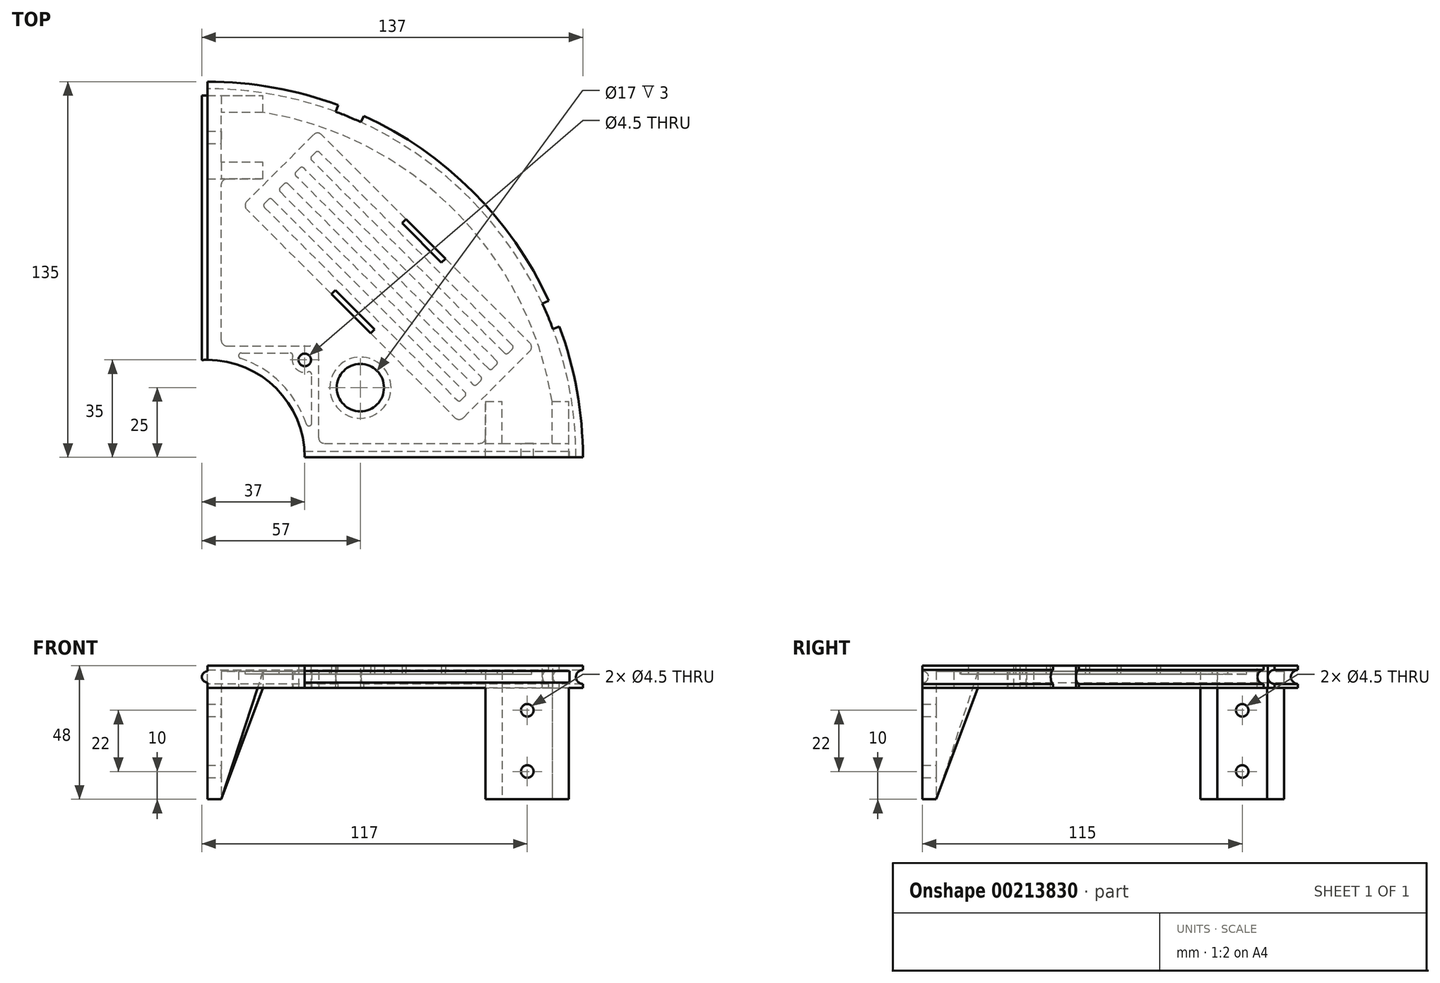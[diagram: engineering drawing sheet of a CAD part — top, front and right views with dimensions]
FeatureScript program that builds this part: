
annotation { "Feature Type Name" : "Feature", "Feature Type Description" : "" }
export const myFeature = defineFeature(function(context is Context, id is Id, definition is map)
    precondition{}
    {
        {
            var Q0;
            Q0=qCreatedBy(makeId("Top.planeOp"),FACE);
            var sketch = newSketch(context, id + "F0", { "sketchPlane" : qUnion([Q0])});
            skArc(sketch, "E0", {"start": v(135, 0) * mm, "mid": v(95.46, 95.46) * mm, "end": v(0, 135) * mm});
            skArc(sketch, "E1", {"start": v(35, 0) * mm, "mid": v(24.75, 24.75) * mm, "end": v(0, 35) * mm});
            skLineSegment(sketch, "E2.trimOffspring", {"start": v(35, 0) * mm, "end": v(135, 0) * mm});
            skLineSegment(sketch, "E3.1.5", {"start": v(0, 35) * mm, "end": v(0, 135) * mm});
            skCircle(sketch, "E4", {"center": v(35, 35) * mm, "radius": 2.25 * mm});
            skSolve(sketch);
        }
        {
            var Q0;
            Q0=qSketchRegion(id+"F0",true);
            extrude(context, id + "F1", {"entities" : qUnion([Q0]), "depth" : 8 * mm});
        }
        {
            var Q0;
            Q0=qCreatedBy(makeId("Top.planeOp"),FACE);
            cPlane(context, id + "F2", {"entities" : qUnion([Q0]), "cplaneType" : CPlaneType.OFFSET, "offset" : 4 * mm, "width" : 150 * mm, "height" : 150 * mm});
        }
        {
            var Q0;
            Q0=qCreatedBy(id+"F2.planeOp",FACE);
            var sketch = newSketch(context, id + "F3", { "sketchPlane" : qUnion([Q0])});
            skCircle(sketch, "E5", {"center": v(0, 0) * mm, "radius": 135 * mm});
            skSolve(sketch);
        }
        {
            var Q0;
            Q0=makeQuery(id+"F1.opExtrude","SWEPT_FACE",FACE,{"disambiguationData":[OSD([sQuery(id+"F0.wireOp",EDGE,"E2.trimOffspring")])]});
            var sketch = newSketch(context, id + "F4", { "sketchPlane" : qUnion([Q0])});
            skCircle(sketch, "E6", {"center": v(135, 4) * mm, "radius": 2.5 * mm});
            skSolve(sketch);
        }
        {
            var Q0;
            Q0=qSketchRegion(id+"F4",true);
            var Q1;
            Q1=qConstructionFilter(qBodyType(qCreatedBy(id+"F3",EDGE),BodyType.WIRE),ConstructionObject.NO);
            sweep(context, id + "F5", {"operationType" : NewBodyOperationType.REMOVE, "profiles" : qUnion([Q0]), "path" : qUnion([Q1])});
        }
        {
            var Q0;
            Q0=makeQuery(id+"F1.opExtrude","CAP_FACE",FACE,{"disambiguationData":[OSD([sQuery(id+"F0.wireOp",EDGE,"E0"),sQuery(id+"F0.wireOp",EDGE,"E1"),sQuery(id+"F0.wireOp",EDGE,"E2.trimOffspring"),sQuery(id+"F0.wireOp",EDGE,"E3.1.5"),sQuery(id+"F0.wireOp",EDGE,"E4")])],"isStart":true});
            var sketch = newSketch(context, id + "F6", { "sketchPlane" : qUnion([Q0])});
            skLineSegment(sketch, "E7.bottom", {"start": v(100, 0) * mm, "end": v(130, 0) * mm});
            skLineSegment(sketch, "E7.top", {"start": v(100, -20) * mm, "end": v(130, -20) * mm});
            skLineSegment(sketch, "E7.left", {"start": v(100, 0) * mm, "end": v(100, -20) * mm});
            skLineSegment(sketch, "E7.right", {"start": v(130, 0) * mm, "end": v(130, -20) * mm});
            skLineSegment(sketch, "E8.bottom", {"start": v(0, -100) * mm, "end": v(20, -100) * mm});
            skLineSegment(sketch, "E8.top", {"start": v(0, -130) * mm, "end": v(20, -130) * mm});
            skLineSegment(sketch, "E8.left", {"start": v(0, -100) * mm, "end": v(0, -130) * mm});
            skLineSegment(sketch, "E8.right", {"start": v(20, -100) * mm, "end": v(20, -130) * mm});
            skSolve(sketch);
        }
        {
            var Q0;
            Q0=qSketchRegion(id+"F6",true);
            extrude(context, id + "F7", {"entities" : qUnion([Q0]), "operationType" : NewBodyOperationType.ADD, "depth" : 40 * mm});
        }
        {
            var Q0;
            Q0=makeQuery(id+"F7.opExtrude","CAP_FACE",FACE,{"disambiguationData":[OSD([sQuery(id+"F6.wireOp",EDGE,"E7.bottom"),sQuery(id+"F6.wireOp",EDGE,"E7.top"),sQuery(id+"F6.wireOp",EDGE,"E7.left"),sQuery(id+"F6.wireOp",EDGE,"E7.right")])],"isStart":false});
            var sketch = newSketch(context, id + "F8", { "sketchPlane" : qUnion([Q0])});
            skLineSegment(sketch, "E9.bottom", {"start": v(106, -5) * mm, "end": v(124, -5) * mm});
            skLineSegment(sketch, "E9.top", {"start": v(106, -20) * mm, "end": v(124, -20) * mm});
            skLineSegment(sketch, "E9.left", {"start": v(106, -5) * mm, "end": v(106, -20) * mm});
            skLineSegment(sketch, "E9.right", {"start": v(124, -5) * mm, "end": v(124, -20) * mm});
            skLineSegment(sketch, "E10.bottom", {"start": v(20, -106) * mm, "end": v(5, -106) * mm});
            skLineSegment(sketch, "E10.top", {"start": v(20, -124) * mm, "end": v(5, -124) * mm});
            skLineSegment(sketch, "E10.left", {"start": v(20, -106) * mm, "end": v(20, -124) * mm});
            skLineSegment(sketch, "E10.right", {"start": v(5, -106) * mm, "end": v(5, -124) * mm});
            skSolve(sketch);
        }
        {
            var Q0;
            Q0=qSketchRegion(id+"F8",true);
            extrude(context, id + "F9", {"entities" : qUnion([Q0]), "operationType" : NewBodyOperationType.REMOVE, "oppositeDirection" : true, "depth" : 40 * mm});
        }
        {
            var Q0;
            {var subQ0=sQuery(id+"F6.wireOp",EDGE,"E7.right");var subQ1=sQuery(id+"F6.wireOp",EDGE,"E7.top");Q0=makeQuery(id+"F9.boolean.opBoolean","SPLIT",EDGE,{"disambiguationData":[TD([makeQuery(id+"F7.opExtrude","SWEPT_FACE",FACE,{"disambiguationData":[OSD([subQ0])]})])],"derivedFrom":makeQuery(id+"F7.opExtrude","CAP_EDGE",EDGE,{"disambiguationData":[OSD([subQ1])],"isStart":false})});}
            chamfer(context, id + "F10", {"entities" : qUnion([Q0]), "chamferType" : ChamferType.TWO_OFFSETS, "width1" : 15 * mm, "oppositeDirection" : false, "width2" : 40 * mm, "tangentPropagation" : true});
        }
        {
            var Q0;
            Q0=makeQuery(id+"F9.boolean.opBoolean","COPY",FACE,{"derivedFrom":makeQuery(id+"F9.opExtrude","SWEPT_FACE",FACE,{"disambiguationData":[OSD([sQuery(id+"F8.wireOp",EDGE,"E9.bottom")])]})});
            var sketch = newSketch(context, id + "F11", { "sketchPlane" : qUnion([Q0])});
            skCircle(sketch, "E11", {"center": v(-115, -8) * mm, "radius": 2.25 * mm});
            skCircle(sketch, "E12", {"center": v(-115, -30) * mm, "radius": 2.25 * mm});
            skSolve(sketch);
        }
        {
            var Q0;
            Q0=qSketchRegion(id+"F11",true);
            extrude(context, id + "F12", {"entities" : qUnion([Q0]), "operationType" : NewBodyOperationType.REMOVE, "oppositeDirection" : true, "depth" : 25 * mm});
        }
        {
            var Q0;
            {var subQ0=sQuery(id+"F6.wireOp",EDGE,"E8.right");var subQ1=sQuery(id+"F6.wireOp",EDGE,"E8.top");Q0=makeQuery(id+"F9.boolean.opBoolean","SPLIT",EDGE,{"disambiguationData":[TD([makeQuery(id+"F7.opExtrude","SWEPT_FACE",FACE,{"disambiguationData":[OSD([subQ1])]})])],"derivedFrom":makeQuery(id+"F7.opExtrude","CAP_EDGE",EDGE,{"disambiguationData":[OSD([subQ0])],"isStart":false})});}
            chamfer(context, id + "F13", {"entities" : qUnion([Q0]), "chamferType" : ChamferType.TWO_OFFSETS, "width1" : 40 * mm, "oppositeDirection" : false, "width2" : 15 * mm, "tangentPropagation" : true});
        }
        {
            var Q0;
            Q0=makeQuery(id+"F9.boolean.opBoolean","COPY",FACE,{"derivedFrom":makeQuery(id+"F9.opExtrude","SWEPT_FACE",FACE,{"disambiguationData":[OSD([sQuery(id+"F8.wireOp",EDGE,"E10.right")])]})});
            var sketch = newSketch(context, id + "F14", { "sketchPlane" : qUnion([Q0])});
            skCircle(sketch, "E13", {"center": v(115, -30) * mm, "radius": 2.25 * mm});
            skCircle(sketch, "E14", {"center": v(115, -8) * mm, "radius": 2.25 * mm});
            skSolve(sketch);
        }
        {
            var Q0;
            Q0=qSketchRegion(id+"F14",true);
            extrude(context, id + "F15", {"entities" : qUnion([Q0]), "operationType" : NewBodyOperationType.REMOVE, "oppositeDirection" : true, "depth" : 25 * mm});
        }
        {
            var Q0;
            Q0=makeQuery(id+"F1.opExtrude","CAP_FACE",FACE,{"disambiguationData":[OSD([sQuery(id+"F0.wireOp",EDGE,"E0"),sQuery(id+"F0.wireOp",EDGE,"E1"),sQuery(id+"F0.wireOp",EDGE,"E2.trimOffspring"),sQuery(id+"F0.wireOp",EDGE,"E3.1.5"),sQuery(id+"F0.wireOp",EDGE,"E4")])],"isStart":false});
            var sketch = newSketch(context, id + "F16", { "sketchPlane" : qUnion([Q0])});
            skArc(sketch, "E15", {"start": v(124.2, 46.14) * mm, "mid": v(122.41, 50.71) * mm, "end": v(120.45, 55.2) * mm});
            skArc(sketch, "E16", {"start": v(126.55, 47.01) * mm, "mid": v(124.72, 51.67) * mm, "end": v(122.72, 56.25) * mm});
            skLineSegment(sketch, "E17", {"start": v(0, 0) * mm, "end": v(124.72, 51.66) * mm, "construction": true});
            skLineSegment(sketch, "E18", {"start": v(0, 0) * mm, "end": v(51.66, 124.72) * mm, "construction": true});
            skLineSegment(sketch, "E19", {"start": v(46.13, 124.21) * mm, "end": v(47, 126.55) * mm});
            skLineSegment(sketch, "E20", {"start": v(124.2, 46.14) * mm, "end": v(126.55, 47.01) * mm});
            skLineSegment(sketch, "E21", {"start": v(55.2, 120.45) * mm, "end": v(56.24, 122.73) * mm});
            skLineSegment(sketch, "E22", {"start": v(120.45, 55.2) * mm, "end": v(122.72, 56.25) * mm});
            skArc(sketch, "E23.trimOffspring", {"start": v(56.24, 122.73) * mm, "mid": v(51.66, 124.73) * mm, "end": v(47, 126.55) * mm});
            skArc(sketch, "E24.trimOffspring", {"start": v(55.2, 120.45) * mm, "mid": v(50.7, 122.42) * mm, "end": v(46.13, 124.21) * mm});
            skSolve(sketch);
        }
        {
            var Q0;
            Q0=qSketchRegion(id+"F16",true);
            extrude(context, id + "F17", {"entities" : qUnion([Q0]), "operationType" : NewBodyOperationType.REMOVE, "oppositeDirection" : true, "depth" : 25 * mm});
        }
        {
            var Q0;
            Q0=makeQuery(id+"F9.boolean.opBoolean","MERGE",FACE,{"derivedFrom":[makeQuery(id+"F1.opExtrude","CAP_FACE",FACE,{"disambiguationData":[OSD([sQuery(id+"F0.wireOp",EDGE,"E0"),sQuery(id+"F0.wireOp",EDGE,"E1"),sQuery(id+"F0.wireOp",EDGE,"E2.trimOffspring"),sQuery(id+"F0.wireOp",EDGE,"E3.1.5"),sQuery(id+"F0.wireOp",EDGE,"E4")])],"isStart":true}),makeQuery(id+"F9.opExtrude","CAP_FACE",FACE,{"disambiguationData":[OSD([sQuery(id+"F8.wireOp",EDGE,"E9.bottom"),sQuery(id+"F8.wireOp",EDGE,"E9.top"),sQuery(id+"F8.wireOp",EDGE,"E9.left"),sQuery(id+"F8.wireOp",EDGE,"E9.right")])],"isStart":false}),makeQuery(id+"F9.opExtrude","CAP_FACE",FACE,{"disambiguationData":[OSD([sQuery(id+"F8.wireOp",EDGE,"E10.bottom"),sQuery(id+"F8.wireOp",EDGE,"E10.top"),sQuery(id+"F8.wireOp",EDGE,"E10.left"),sQuery(id+"F8.wireOp",EDGE,"E10.right")])],"isStart":false})]});
            var sketch = newSketch(context, id + "F18", { "sketchPlane" : qUnion([Q0])});
            skLineSegment(sketch, "E25", {"start": v(0, 0) * mm, "end": v(106.07, -106.07) * mm, "construction": true});
            skLineSegment(sketch, "E26", {"start": v(45.96, -60.1) * mm, "end": v(60.1, -45.96) * mm});
            skLineSegment(sketch, "E27", {"start": v(70, -84.15) * mm, "end": v(84.15, -70) * mm});
            skLineSegment(sketch, "E28", {"start": v(44.55, -58.69) * mm, "end": v(58.69, -44.55) * mm});
            skLineSegment(sketch, "E29", {"start": v(71.42, -85.56) * mm, "end": v(85.56, -71.42) * mm});
            skLineSegment(sketch, "E30", {"start": v(44.55, -58.69) * mm, "end": v(45.96, -60.1) * mm});
            skLineSegment(sketch, "E31", {"start": v(58.69, -44.55) * mm, "end": v(60.1, -45.96) * mm});
            skLineSegment(sketch, "E32", {"start": v(84.15, -70) * mm, "end": v(85.56, -71.42) * mm});
            skLineSegment(sketch, "E33", {"start": v(70, -84.15) * mm, "end": v(71.42, -85.56) * mm});
            skSolve(sketch);
        }
        {
            var Q0;
            Q0=qSketchRegion(id+"F18",true);
            extrude(context, id + "F19", {"entities" : qUnion([Q0]), "operationType" : NewBodyOperationType.REMOVE, "endBound" : BoundingType.THROUGH_ALL, "oppositeDirection" : true, "depth" : 7.8 * mm});
        }
        {
            var Q0;
            Q0=makeQuery(id+"F7.boolean.opBoolean","MERGE",FACE,{"derivedFrom":[makeQuery(id+"F1.opExtrude","SWEPT_FACE",FACE,{"disambiguationData":[OSD([sQuery(id+"F0.wireOp",EDGE,"E2.trimOffspring")])]}),makeQuery(id+"F7.opExtrude","SWEPT_FACE",FACE,{"disambiguationData":[OSD([sQuery(id+"F6.wireOp",EDGE,"E7.bottom")])]})]});
            var sketch = newSketch(context, id + "F20", { "sketchPlane" : qUnion([Q0])});
            skLineSegment(sketch, "E34", {"start": v(0, 4) * mm, "end": v(130.2, 4) * mm});
            skSolve(sketch);
        }
        {
            var Q0;
            Q0=makeQuery(id+"F7.boolean.opBoolean","MERGE",FACE,{"derivedFrom":[makeQuery(id+"F1.opExtrude","SWEPT_FACE",FACE,{"disambiguationData":[OSD([sQuery(id+"F0.wireOp",EDGE,"E3.1.5")])]}),makeQuery(id+"F7.opExtrude","SWEPT_FACE",FACE,{"disambiguationData":[OSD([sQuery(id+"F6.wireOp",EDGE,"E8.left")])]})]});
            var sketch = newSketch(context, id + "F21", { "sketchPlane" : qUnion([Q0])});
            skLineSegment(sketch, "E35", {"start": v(-130, 4) * mm, "end": v(0, 4) * mm});
            skSolve(sketch);
        }
        {
            var Q0;
            Q0=qCreatedBy(makeId("Front.planeOp"),FACE);
            var sketch = newSketch(context, id + "F22", { "sketchPlane" : qUnion([Q0])});
            skCircle(sketch, "E36", {"center": v(0, 4) * mm, "radius": 2 * mm});
            skSolve(sketch);
        }
        {
            var Q0;
            Q0=makeQuery(id+"F22.imprint","IMPRINT",FACE,{"disambiguationData":[TD([[makeQuery(id+"F22.imprint","IMPRINT",EDGE,{"derivedFrom":sQuery(id+"F22.wireOp",EDGE,"E36")}),1.0]])]});
            var Q1;
            Q1=sQuery(id+"F21.wireOp",EDGE,"E35");
            sweep(context, id + "F23", {"operationType" : NewBodyOperationType.ADD, "profiles" : qUnion([Q0]), "path" : qUnion([Q1])});
        }
        {
            var Q0;
            Q0=makeQuery(id+"F1.opExtrude","CAP_FACE",FACE,{"disambiguationData":[OSD([sQuery(id+"F0.wireOp",EDGE,"E0"),sQuery(id+"F0.wireOp",EDGE,"E1"),sQuery(id+"F0.wireOp",EDGE,"E2.trimOffspring"),sQuery(id+"F0.wireOp",EDGE,"E3.1.5"),sQuery(id+"F0.wireOp",EDGE,"E4")])],"isStart":false});
            var sketch = newSketch(context, id + "F24", { "sketchPlane" : qUnion([Q0])});
            skCircle(sketch, "E37", {"center": v(0, 0) * mm, "radius": 35 * mm});
            skSolve(sketch);
        }
        {
            var Q0;
            {var subQ0=sQuery(id+"F24.wireOp",EDGE,"E37");var subQ1=makeQuery(id+"F24.imprint","INTERSECT",VERTEX,{"derivedFrom":[makeQuery(id+"F1.opExtrude","CAP_EDGE",EDGE,{"disambiguationData":[OSD([sQuery(id+"F0.wireOp",EDGE,"E2.trimOffspring")])],"isStart":false}),subQ0]});Q0=makeQuery(id+"F24.imprint","IMPRINT",FACE,{"disambiguationData":[TD([[makeQuery(id+"F24.imprint","IMPRINT",EDGE,{"disambiguationData":[TD([[subQ1,-1.0]])],"derivedFrom":subQ0}),1.0]])]});}
            extrude(context, id + "F25", {"entities" : qUnion([Q0]), "operationType" : NewBodyOperationType.REMOVE, "endBound" : BoundingType.THROUGH_ALL, "oppositeDirection" : true, "depth" : 25 * mm});
        }
        {
            var Q0;
            Q0=qCreatedBy(makeId("Right.planeOp"),FACE);
            var sketch = newSketch(context, id + "F26", { "sketchPlane" : qUnion([Q0])});
            skCircle(sketch, "E38", {"center": v(0, 4) * mm, "radius": 2.1 * mm});
            skSolve(sketch);
        }
        {
            var Q0;
            Q0=makeQuery(id+"F26.imprint","IMPRINT",FACE,{"disambiguationData":[TD([[makeQuery(id+"F26.imprint","IMPRINT",EDGE,{"derivedFrom":sQuery(id+"F26.wireOp",EDGE,"E38")}),1.0]])]});
            var Q1;
            Q1=sQuery(id+"F20.wireOp",EDGE,"E34");
            sweep(context, id + "F27", {"operationType" : NewBodyOperationType.REMOVE, "profiles" : qUnion([Q0]), "path" : qUnion([Q1])});
        }
        {
            var Q0;
            Q0=makeQuery(id+"F9.boolean.opBoolean","MERGE",FACE,{"derivedFrom":[makeQuery(id+"F1.opExtrude","CAP_FACE",FACE,{"disambiguationData":[OSD([sQuery(id+"F0.wireOp",EDGE,"E0"),sQuery(id+"F0.wireOp",EDGE,"E1"),sQuery(id+"F0.wireOp",EDGE,"E2.trimOffspring"),sQuery(id+"F0.wireOp",EDGE,"E3.1.5"),sQuery(id+"F0.wireOp",EDGE,"E4")])],"isStart":true}),makeQuery(id+"F9.opExtrude","CAP_FACE",FACE,{"disambiguationData":[OSD([sQuery(id+"F8.wireOp",EDGE,"E9.bottom"),sQuery(id+"F8.wireOp",EDGE,"E9.top"),sQuery(id+"F8.wireOp",EDGE,"E9.left"),sQuery(id+"F8.wireOp",EDGE,"E9.right")])],"isStart":false}),makeQuery(id+"F9.opExtrude","CAP_FACE",FACE,{"disambiguationData":[OSD([sQuery(id+"F8.wireOp",EDGE,"E10.bottom"),sQuery(id+"F8.wireOp",EDGE,"E10.top"),sQuery(id+"F8.wireOp",EDGE,"E10.left"),sQuery(id+"F8.wireOp",EDGE,"E10.right")])],"isStart":false})]});
            var sketch = newSketch(context, id + "F28", { "sketchPlane" : qUnion([Q0])});
            skCircle(sketch, "E39", {"center": v(55, -25) * mm, "radius": 8.5 * mm});
            skSolve(sketch);
        }
        {
            var Q0;
            Q0=makeQuery(id+"F28.imprint","IMPRINT",FACE,{"disambiguationData":[TD([[makeQuery(id+"F28.imprint","IMPRINT",EDGE,{"derivedFrom":sQuery(id+"F28.wireOp",EDGE,"E39")}),1.0]])]});
            extrude(context, id + "F29", {"entities" : qUnion([Q0]), "operationType" : NewBodyOperationType.REMOVE, "endBound" : BoundingType.THROUGH_ALL, "oppositeDirection" : true, "depth" : 7.6 * mm});
        }
        {
            var Q0;
            Q0=makeQuery(id+"F9.boolean.opBoolean","MERGE",FACE,{"derivedFrom":[makeQuery(id+"F1.opExtrude","CAP_FACE",FACE,{"disambiguationData":[OSD([sQuery(id+"F0.wireOp",EDGE,"E0"),sQuery(id+"F0.wireOp",EDGE,"E1"),sQuery(id+"F0.wireOp",EDGE,"E2.trimOffspring"),sQuery(id+"F0.wireOp",EDGE,"E3.1.5"),sQuery(id+"F0.wireOp",EDGE,"E4")])],"isStart":true}),makeQuery(id+"F9.opExtrude","CAP_FACE",FACE,{"disambiguationData":[OSD([sQuery(id+"F8.wireOp",EDGE,"E9.bottom"),sQuery(id+"F8.wireOp",EDGE,"E9.top"),sQuery(id+"F8.wireOp",EDGE,"E9.left"),sQuery(id+"F8.wireOp",EDGE,"E9.right")])],"isStart":false}),makeQuery(id+"F9.opExtrude","CAP_FACE",FACE,{"disambiguationData":[OSD([sQuery(id+"F8.wireOp",EDGE,"E10.bottom"),sQuery(id+"F8.wireOp",EDGE,"E10.top"),sQuery(id+"F8.wireOp",EDGE,"E10.left"),sQuery(id+"F8.wireOp",EDGE,"E10.right")])],"isStart":false})]});
            var sketch = newSketch(context, id + "F30", { "sketchPlane" : qUnion([Q0])});
            skLineSegment(sketch, "E40.top", {"start": v(7, -40) * mm, "end": v(37, -40) * mm});
            skLineSegment(sketch, "E40.right", {"start": v(40, -7) * mm, "end": v(40, -37) * mm});
            skArc(sketch, "E41", {"start": v(20, -124) * mm, "mid": v(88.81, -88.81) * mm, "end": v(124, -20) * mm});
            skLineSegment(sketch, "E42", {"start": v(106, -20) * mm, "end": v(100, -20) * mm});
            skLineSegment(sketch, "E43", {"start": v(20, -106) * mm, "end": v(20, -100) * mm});
            skLineSegment(sketch, "E44", {"start": v(5, -42) * mm, "end": v(5, -98) * mm});
            skLineSegment(sketch, "E45", {"start": v(7, -100) * mm, "end": v(20, -100) * mm});
            skLineSegment(sketch, "E46", {"start": v(42, -5) * mm, "end": v(98, -5) * mm});
            skLineSegment(sketch, "E47", {"start": v(100, -7) * mm, "end": v(100, -20) * mm});
            skPoint(sketch, "E48.visualSharp", {"position": v(40, -40) * mm});
            skArc(sketch, "E48.filletArc", {"start": v(37, -40) * mm, "mid": v(39.12, -39.12) * mm, "end": v(40, -37) * mm});
            skArc(sketch, "E49.filletArc", {"start": v(7, -40) * mm, "mid": v(5.59, -40.59) * mm, "end": v(5, -42) * mm});
            skArc(sketch, "E50.filletArc", {"start": v(42, -5) * mm, "mid": v(40.59, -5.59) * mm, "end": v(40, -7) * mm});
            skPoint(sketch, "E51.visualSharp", {"position": v(5, -100) * mm});
            skArc(sketch, "E51.filletArc", {"start": v(5, -98) * mm, "mid": v(5.59, -99.41) * mm, "end": v(7, -100) * mm});
            skPoint(sketch, "E52.visualSharp", {"position": v(100, -5) * mm});
            skArc(sketch, "E52.filletArc", {"start": v(100, -7) * mm, "mid": v(99.41, -5.59) * mm, "end": v(98, -5) * mm});
            skLineSegment(sketch, "E53", {"start": v(20, -124) * mm, "end": v(5, -124) * mm});
            skLineSegment(sketch, "E54", {"start": v(5, -124) * mm, "end": v(5, -106) * mm});
            skLineSegment(sketch, "E55", {"start": v(5, -106) * mm, "end": v(20, -106) * mm});
            skLineSegment(sketch, "E56", {"start": v(106, -20) * mm, "end": v(106, -5) * mm});
            skLineSegment(sketch, "E57", {"start": v(106, -5) * mm, "end": v(124, -5) * mm});
            skLineSegment(sketch, "E58", {"start": v(124, -5) * mm, "end": v(124, -20) * mm});
            skArc(sketch, "E59", {"start": v(11.93, -35.55) * mm, "mid": v(26.52, -26.52) * mm, "end": v(35.55, -11.93) * mm});
            skLineSegment(sketch, "E60.top", {"start": v(12.25, -37.5) * mm, "end": v(29.7, -37.5) * mm});
            skLineSegment(sketch, "E60.right", {"start": v(37.5, -12.25) * mm, "end": v(37.5, -29.7) * mm});
            skArc(sketch, "E61", {"start": v(36.23, -30.67) * mm, "mid": v(31.82, -31.82) * mm, "end": v(30.67, -36.23) * mm});
            skPoint(sketch, "E62.visualSharp", {"position": v(0, -37.5) * mm});
            skArc(sketch, "E62.filletArc", {"start": v(11.93, -35.55) * mm, "mid": v(11.26, -36.66) * mm, "end": v(12.25, -37.5) * mm});
            skPoint(sketch, "E63.visualSharp", {"position": v(37.5, 0) * mm});
            skArc(sketch, "E63.filletArc", {"start": v(37.5, -12.25) * mm, "mid": v(36.66, -11.26) * mm, "end": v(35.55, -11.93) * mm});
            skPoint(sketch, "E64.visualSharp", {"position": v(31.26, -37.5) * mm});
            skArc(sketch, "E64.filletArc", {"start": v(29.7, -37.5) * mm, "mid": v(30.5, -37.1) * mm, "end": v(30.67, -36.23) * mm});
            skPoint(sketch, "E65.visualSharp", {"position": v(37.5, -31.26) * mm});
            skArc(sketch, "E65.filletArc", {"start": v(36.23, -30.67) * mm, "mid": v(37.1, -30.5) * mm, "end": v(37.5, -29.7) * mm});
            skSolve(sketch);
        }
        {
            var Q0;
            Q0=qSketchRegion(id+"F30",true);
            extrude(context, id + "F31", {"entities" : qUnion([Q0]), "operationType" : NewBodyOperationType.REMOVE, "oppositeDirection" : true, "depth" : 6 * mm});
        }
        {
            var Q0;
            {var subQ0=sQuery(id+"F6.wireOp",EDGE,"E8.bottom");var subQ1=sQuery(id+"F6.wireOp",EDGE,"E8.right");Q0=makeQuery(id+"F9.boolean.opBoolean","SPLIT",EDGE,{"disambiguationData":[TD([makeQuery(id+"F7.opExtrude","SWEPT_FACE",FACE,{"disambiguationData":[OSD([subQ0])]})])],"derivedFrom":makeQuery(id+"F7.opExtrude","CAP_EDGE",EDGE,{"disambiguationData":[OSD([subQ1])],"isStart":false})});}
            chamfer(context, id + "F32", {"entities" : qUnion([Q0]), "chamferType" : ChamferType.TWO_OFFSETS, "width1" : 46 * mm, "oppositeDirection" : false, "width2" : 15 * mm, "tangentPropagation" : true});
        }
        {
            var Q0;
            {var subQ0=sQuery(id+"F6.wireOp",EDGE,"E7.left");var subQ1=sQuery(id+"F6.wireOp",EDGE,"E7.top");Q0=makeQuery(id+"F9.boolean.opBoolean","SPLIT",EDGE,{"disambiguationData":[TD([makeQuery(id+"F7.opExtrude","SWEPT_FACE",FACE,{"disambiguationData":[OSD([subQ0])]})])],"derivedFrom":makeQuery(id+"F7.opExtrude","CAP_EDGE",EDGE,{"disambiguationData":[OSD([subQ1])],"isStart":false})});}
            chamfer(context, id + "F33", {"entities" : qUnion([Q0]), "chamferType" : ChamferType.TWO_OFFSETS, "width1" : 15 * mm, "oppositeDirection" : false, "width2" : 46 * mm, "tangentPropagation" : true});
        }
        {
            var Q0;
            Q0=makeQuery(id+"F31.boolean.opBoolean","COPY",FACE,{"derivedFrom":makeQuery(id+"F31.opExtrude","CAP_FACE",FACE,{"disambiguationData":[OSD([sQuery(id+"F30.wireOp",EDGE,"E40.top"),sQuery(id+"F30.wireOp",EDGE,"E40.right"),sQuery(id+"F30.wireOp",EDGE,"E41"),sQuery(id+"F30.wireOp",EDGE,"E42"),sQuery(id+"F30.wireOp",EDGE,"E43"),sQuery(id+"F30.wireOp",EDGE,"E44"),sQuery(id+"F30.wireOp",EDGE,"E45"),sQuery(id+"F30.wireOp",EDGE,"E46"),sQuery(id+"F30.wireOp",EDGE,"E47"),sQuery(id+"F30.wireOp",EDGE,"E48.filletArc"),sQuery(id+"F30.wireOp",EDGE,"E49.filletArc"),sQuery(id+"F30.wireOp",EDGE,"E50.filletArc"),sQuery(id+"F30.wireOp",EDGE,"E51.filletArc"),sQuery(id+"F30.wireOp",EDGE,"E52.filletArc"),sQuery(id+"F30.wireOp",EDGE,"E53"),sQuery(id+"F30.wireOp",EDGE,"E54"),sQuery(id+"F30.wireOp",EDGE,"E55"),sQuery(id+"F30.wireOp",EDGE,"E56"),sQuery(id+"F30.wireOp",EDGE,"E57"),sQuery(id+"F30.wireOp",EDGE,"E58")])],"isStart":false})});
            var sketch = newSketch(context, id + "F34", { "sketchPlane" : qUnion([Q0])});
            skLineSegment(sketch, "E66", {"start": v(71.42, -85.56) * mm, "end": v(41.01, -115.97) * mm});
            skLineSegment(sketch, "E67", {"start": v(38.18, -115.97) * mm, "end": v(14.14, -91.92) * mm});
            skLineSegment(sketch, "E68", {"start": v(44.55, -58.69) * mm, "end": v(14.14, -89.1) * mm});
            skLineSegment(sketch, "E69", {"start": v(44.55, -58.69) * mm, "end": v(45.96, -60.1) * mm});
            skLineSegment(sketch, "E70", {"start": v(45.96, -60.1) * mm, "end": v(60.1, -45.96) * mm});
            skLineSegment(sketch, "E71", {"start": v(60.1, -45.96) * mm, "end": v(58.69, -44.55) * mm});
            skLineSegment(sketch, "E72", {"start": v(58.69, -44.55) * mm, "end": v(89.1, -14.14) * mm});
            skLineSegment(sketch, "E73", {"start": v(91.92, -14.14) * mm, "end": v(115.97, -38.18) * mm});
            skLineSegment(sketch, "E74", {"start": v(71.42, -85.56) * mm, "end": v(70, -84.15) * mm});
            skLineSegment(sketch, "E75", {"start": v(70, -84.15) * mm, "end": v(84.15, -70) * mm});
            skLineSegment(sketch, "E76", {"start": v(84.15, -70) * mm, "end": v(85.56, -71.42) * mm});
            skLineSegment(sketch, "E77", {"start": v(85.56, -71.42) * mm, "end": v(115.97, -41.01) * mm});
            skLineSegment(sketch, "E78", {"start": v(53.03, -53.03) * mm, "end": v(77.07, -77.07) * mm, "construction": true});
            skCircle(sketch, "E79", {"center": v(55, -25) * mm, "radius": 11 * mm});
            skCircle(sketch, "E80", {"center": v(55, -25) * mm, "radius": 8.5 * mm});
            skPoint(sketch, "E81.visualSharp", {"position": v(90.5, -12.73) * mm});
            skArc(sketch, "E81.filletArc", {"start": v(91.92, -14.14) * mm, "mid": v(90.5, -13.56) * mm, "end": v(89.1, -14.14) * mm});
            skPoint(sketch, "E82.visualSharp", {"position": v(117.38, -39.6) * mm});
            skArc(sketch, "E82.filletArc", {"start": v(115.97, -41.01) * mm, "mid": v(116.55, -39.6) * mm, "end": v(115.97, -38.18) * mm});
            skPoint(sketch, "E83.visualSharp", {"position": v(12.73, -90.5) * mm});
            skArc(sketch, "E83.filletArc", {"start": v(14.14, -89.1) * mm, "mid": v(13.56, -90.5) * mm, "end": v(14.14, -91.92) * mm});
            skPoint(sketch, "E84.visualSharp", {"position": v(39.6, -117.38) * mm});
            skArc(sketch, "E84.filletArc", {"start": v(38.18, -115.97) * mm, "mid": v(39.6, -116.55) * mm, "end": v(41.01, -115.97) * mm});
            skLineSegment(sketch, "E85", {"start": v(91.22, -20.5) * mm, "end": v(92.63, -21.92) * mm});
            skLineSegment(sketch, "E86", {"start": v(109.6, -40.3) * mm, "end": v(40.3, -109.6) * mm});
            skLineSegment(sketch, "E87", {"start": v(38.9, -109.6) * mm, "end": v(37.48, -108.19) * mm});
            skLineSegment(sketch, "E88", {"start": v(20.5, -89.8) * mm, "end": v(89.8, -20.5) * mm});
            skLineSegment(sketch, "E89", {"start": v(23.33, -92.63) * mm, "end": v(92.63, -23.33) * mm});
            skLineSegment(sketch, "E90", {"start": v(106.77, -37.48) * mm, "end": v(37.48, -106.77) * mm});
            skLineSegment(sketch, "E91", {"start": v(26.16, -95.46) * mm, "end": v(95.46, -26.16) * mm});
            skLineSegment(sketch, "E92", {"start": v(103.94, -34.65) * mm, "end": v(34.65, -103.94) * mm});
            skLineSegment(sketch, "E93", {"start": v(29, -98.29) * mm, "end": v(98.29, -29) * mm});
            skLineSegment(sketch, "E94", {"start": v(101.12, -31.82) * mm, "end": v(31.82, -101.12) * mm});
            skLineSegment(sketch, "E95.trimOffspring", {"start": v(21.92, -92.63) * mm, "end": v(20.5, -91.22) * mm});
            skLineSegment(sketch, "E96.trimOffspring", {"start": v(33.23, -103.94) * mm, "end": v(31.82, -102.53) * mm});
            skLineSegment(sketch, "E97.trimOffspring", {"start": v(27.58, -98.29) * mm, "end": v(26.16, -96.87) * mm});
            skLineSegment(sketch, "E98.trimOffspring", {"start": v(108.19, -37.48) * mm, "end": v(109.6, -38.9) * mm});
            skLineSegment(sketch, "E99.trimOffspring", {"start": v(102.53, -31.82) * mm, "end": v(103.94, -33.23) * mm});
            skLineSegment(sketch, "E100.trimOffspring", {"start": v(96.87, -26.16) * mm, "end": v(98.29, -27.58) * mm});
            skPoint(sketch, "E101.visualSharp", {"position": v(19.8, -90.5) * mm});
            skArc(sketch, "E101.filletArc", {"start": v(20.5, -89.8) * mm, "mid": v(20.21, -90.5) * mm, "end": v(20.5, -91.22) * mm});
            skPoint(sketch, "E102.visualSharp", {"position": v(22.63, -93.34) * mm});
            skArc(sketch, "E102.filletArc", {"start": v(21.92, -92.63) * mm, "mid": v(22.63, -92.92) * mm, "end": v(23.33, -92.63) * mm});
            skPoint(sketch, "E103.visualSharp", {"position": v(25.46, -96.17) * mm});
            skArc(sketch, "E103.filletArc", {"start": v(26.16, -95.46) * mm, "mid": v(25.87, -96.17) * mm, "end": v(26.16, -96.87) * mm});
            skPoint(sketch, "E104.visualSharp", {"position": v(28.28, -99) * mm});
            skArc(sketch, "E104.filletArc", {"start": v(27.58, -98.29) * mm, "mid": v(28.28, -98.58) * mm, "end": v(29, -98.29) * mm});
            skPoint(sketch, "E105.visualSharp", {"position": v(31.11, -101.82) * mm});
            skArc(sketch, "E105.filletArc", {"start": v(31.82, -101.12) * mm, "mid": v(31.53, -101.82) * mm, "end": v(31.82, -102.53) * mm});
            skPoint(sketch, "E106.visualSharp", {"position": v(33.94, -104.65) * mm});
            skArc(sketch, "E106.filletArc", {"start": v(33.23, -103.94) * mm, "mid": v(33.94, -104.24) * mm, "end": v(34.65, -103.94) * mm});
            skPoint(sketch, "E107.visualSharp", {"position": v(36.77, -107.48) * mm});
            skArc(sketch, "E107.filletArc", {"start": v(37.48, -106.77) * mm, "mid": v(37.18, -107.48) * mm, "end": v(37.48, -108.19) * mm});
            skPoint(sketch, "E108.visualSharp", {"position": v(39.6, -110.3) * mm});
            skArc(sketch, "E108.filletArc", {"start": v(38.9, -109.6) * mm, "mid": v(39.6, -109.9) * mm, "end": v(40.3, -109.6) * mm});
            skPoint(sketch, "E109.visualSharp", {"position": v(110.3, -39.6) * mm});
            skArc(sketch, "E109.filletArc", {"start": v(109.6, -40.3) * mm, "mid": v(109.9, -39.6) * mm, "end": v(109.6, -38.9) * mm});
            skPoint(sketch, "E110.visualSharp", {"position": v(107.48, -36.77) * mm});
            skArc(sketch, "E110.filletArc", {"start": v(108.19, -37.48) * mm, "mid": v(107.48, -37.18) * mm, "end": v(106.77, -37.48) * mm});
            skPoint(sketch, "E111.visualSharp", {"position": v(104.65, -33.94) * mm});
            skArc(sketch, "E111.filletArc", {"start": v(103.94, -34.65) * mm, "mid": v(104.24, -33.94) * mm, "end": v(103.94, -33.23) * mm});
            skPoint(sketch, "E112.visualSharp", {"position": v(101.82, -31.11) * mm});
            skArc(sketch, "E112.filletArc", {"start": v(102.53, -31.82) * mm, "mid": v(101.82, -31.53) * mm, "end": v(101.12, -31.82) * mm});
            skPoint(sketch, "E113.visualSharp", {"position": v(99, -28.28) * mm});
            skArc(sketch, "E113.filletArc", {"start": v(98.29, -29) * mm, "mid": v(98.58, -28.28) * mm, "end": v(98.29, -27.58) * mm});
            skPoint(sketch, "E114.visualSharp", {"position": v(96.17, -25.46) * mm});
            skArc(sketch, "E114.filletArc", {"start": v(96.87, -26.16) * mm, "mid": v(96.17, -25.87) * mm, "end": v(95.46, -26.16) * mm});
            skPoint(sketch, "E115.visualSharp", {"position": v(90.5, -19.8) * mm});
            skArc(sketch, "E115.filletArc", {"start": v(91.22, -20.5) * mm, "mid": v(90.5, -20.21) * mm, "end": v(89.8, -20.5) * mm});
            skPoint(sketch, "E116.visualSharp", {"position": v(93.34, -22.63) * mm});
            skArc(sketch, "E116.filletArc", {"start": v(92.63, -23.33) * mm, "mid": v(92.92, -22.63) * mm, "end": v(92.63, -21.92) * mm});
            skSolve(sketch);
        }
        {
            var Q0;
            Q0 = qSketchRegion(id + "F34", true);
            extrude(context, id + "F35", {"entities" : qUnion([Q0]), "operationType" : NewBodyOperationType.ADD, "depth" : 1 * mm});
        }
    });
